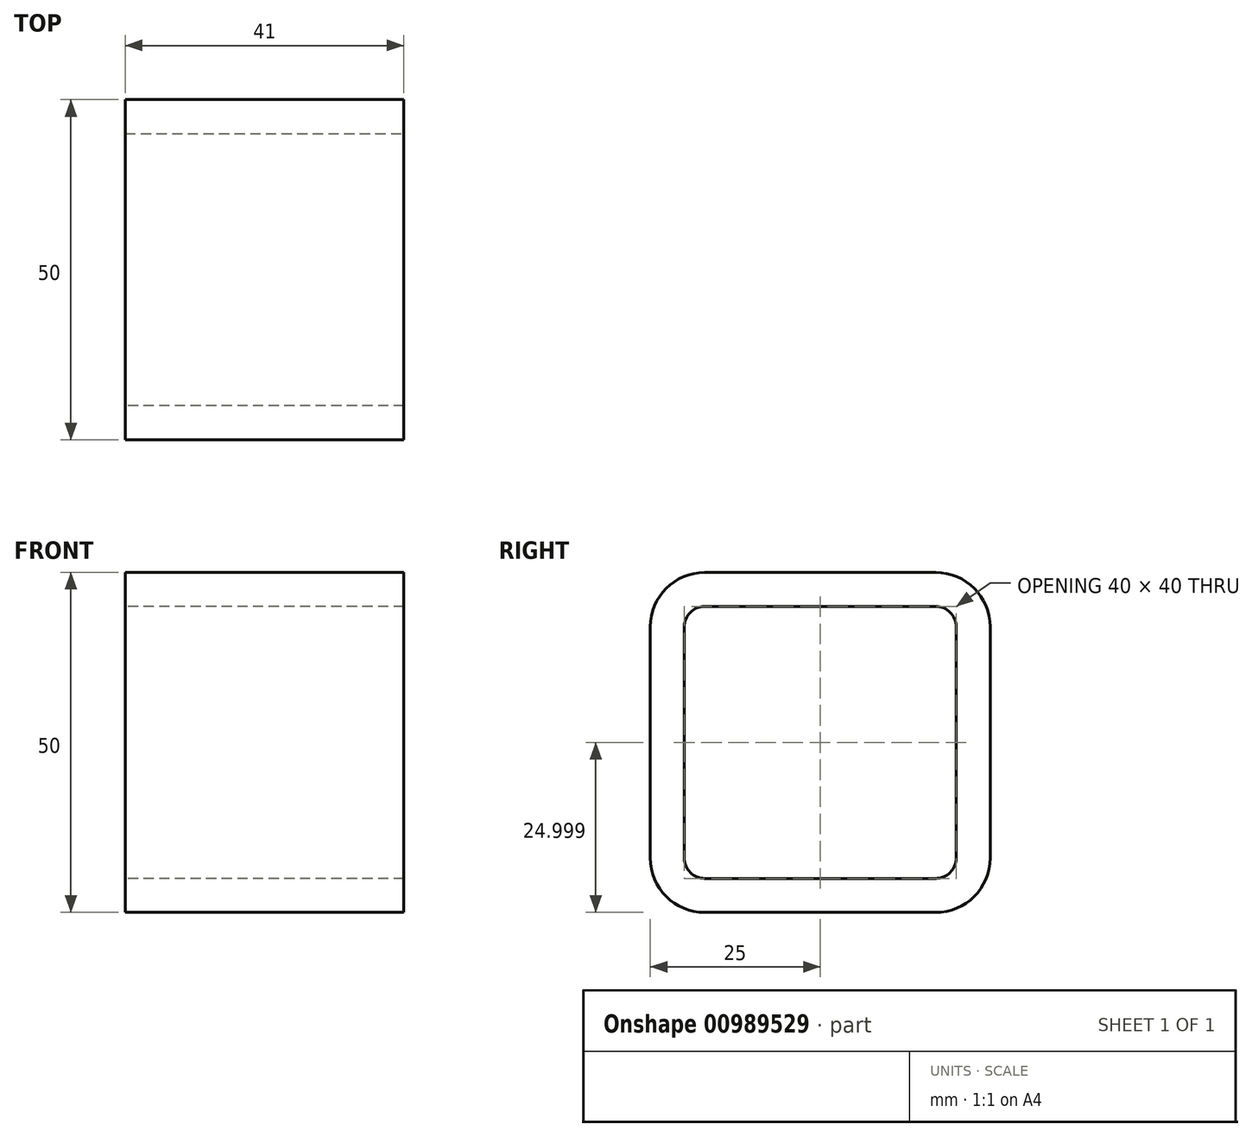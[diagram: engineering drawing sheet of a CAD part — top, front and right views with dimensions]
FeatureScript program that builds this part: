
annotation { "Feature Type Name" : "Feature", "Feature Type Description" : "" }
export const myFeature = defineFeature(function(context is Context, id is Id, definition is map)
    precondition{}
    {
        {
            var Q0;
            Q0=qCreatedBy(makeId("Right.planeOp"),FACE);
            var sketch = newSketch(context, id + "F0", { "sketchPlane" : qUnion([Q0])});
            skPoint(sketch, "E0.visualSharp", {"position": v(-30, 19.07) * mm});
            skPoint(sketch, "E1.visualSharp", {"position": v(20, 19.07) * mm});
            skPoint(sketch, "E2.visualSharp", {"position": v(20, -30.93) * mm});
            skPoint(sketch, "E3.visualSharp", {"position": v(-30, -30.93) * mm});
            skPoint(sketch, "E4.start.orphan", {"position": v(22, 25.88) * mm});
            skPoint(sketch, "E5.end.orphan", {"position": v(-25, -22) * mm});
            skPoint(sketch, "E5.start.orphan", {"position": v(-25, 22) * mm});
            skPoint(sketch, "E6.end.orphan", {"position": v(-22, -25) * mm});
            skPoint(sketch, "E6.start.orphan", {"position": v(12.4, -25) * mm});
            skPoint(sketch, "E7.start.orphan", {"position": v(25.62, 22) * mm});
            skPoint(sketch, "E1.filletArc.center.orphan", {"position": v(22, 22) * mm});
            skPoint(sketch, "E0.filletArc.center.orphan", {"position": v(-22, 22) * mm});
            skPoint(sketch, "E3.filletArc.center.orphan", {"position": v(-22, -22) * mm});
            skLineSegment(sketch, "E8.right", {"start": v(20, 11.07) * mm, "end": v(20, -22.93) * mm});
            skPoint(sketch, "E9.trimOffspring.start.orphan", {"position": v(22, 30) * mm});
            skPoint(sketch, "E10.trimOffspring.start.orphan", {"position": v(12.4, -30) * mm});
            skPoint(sketch, "E8.top.end.orphan", {"position": v(-22, -30) * mm});
            skLineSegment(sketch, "E11", {"start": v(12, 19.07) * mm, "end": v(-22, 19.07) * mm});
            skLineSegment(sketch, "E12", {"start": v(-22, -30.93) * mm, "end": v(12, -30.93) * mm});
            skLineSegment(sketch, "E13", {"start": v(-30, 11.07) * mm, "end": v(-30, -22.93) * mm});
            skLineSegment(sketch, "E14.bottom", {"start": v(-25, 14.07) * mm, "end": v(-25, 14.07) * mm});
            skLineSegment(sketch, "E14.top", {"start": v(-25, -25.93) * mm, "end": v(-25, -25.93) * mm});
            skLineSegment(sketch, "E14.left", {"start": v(-25, 11.07) * mm, "end": v(-25, -22.93) * mm});
            skLineSegment(sketch, "E14.right", {"start": v(-25, 11.07) * mm, "end": v(-25, -22.93) * mm});
            skLineSegment(sketch, "E15.bottom", {"start": v(-22, -25.93) * mm, "end": v(12, -25.93) * mm});
            skLineSegment(sketch, "E16.bottom", {"start": v(15, -25) * mm, "end": v(15, -25) * mm});
            skLineSegment(sketch, "E16.top", {"start": v(15, 14.07) * mm, "end": v(15, 14.07) * mm});
            skLineSegment(sketch, "E16.left", {"start": v(15, -22.93) * mm, "end": v(15, 11.07) * mm});
            skLineSegment(sketch, "E16.right", {"start": v(15, -22.93) * mm, "end": v(15, 11.07) * mm});
            skLineSegment(sketch, "E17.bottom", {"start": v(-22, 14.07) * mm, "end": v(12, 14.07) * mm});
            skLineSegment(sketch, "E17.top", {"start": v(-22, 14.07) * mm, "end": v(12, 14.07) * mm});
            skPoint(sketch, "E18.visualSharp", {"position": v(-25, 14.07) * mm});
            skArc(sketch, "E18.filletArc", {"start": v(-22, 14.07) * mm, "mid": v(-24.12, 13.2) * mm, "end": v(-25, 11.07) * mm});
            skPoint(sketch, "E19.visualSharp", {"position": v(15, 14.07) * mm});
            skArc(sketch, "E19.filletArc", {"start": v(15, 11.07) * mm, "mid": v(14.12, 13.2) * mm, "end": v(12, 14.07) * mm});
            skPoint(sketch, "E20.visualSharp", {"position": v(-25, -25.93) * mm});
            skArc(sketch, "E20.filletArc", {"start": v(-25, -22.93) * mm, "mid": v(-24.12, -25.05) * mm, "end": v(-22, -25.93) * mm});
            skArc(sketch, "E21.filletArc", {"start": v(12, -25.93) * mm, "mid": v(14.12, -25.05) * mm, "end": v(15, -22.93) * mm});
            skArc(sketch, "E22.filletArc", {"start": v(-22, 19.07) * mm, "mid": v(-27.66, 16.73) * mm, "end": v(-30, 11.07) * mm});
            skArc(sketch, "E23.filletArc", {"start": v(-30, -22.93) * mm, "mid": v(-27.66, -28.59) * mm, "end": v(-22, -30.93) * mm});
            skArc(sketch, "E24.filletArc", {"start": v(12, -30.93) * mm, "mid": v(17.66, -28.59) * mm, "end": v(20, -22.93) * mm});
            skArc(sketch, "E25.filletArc", {"start": v(20, 11.07) * mm, "mid": v(17.66, 16.73) * mm, "end": v(12, 19.07) * mm});
            skSolve(sketch);
        }
        {
            var Q0;
            Q0=makeQuery(id+"F0.imprint","IMPRINT",FACE,{"disambiguationData":[TD([[makeQuery(id+"F0.imprint","IMPRINT",EDGE,{"derivedFrom":sQuery(id+"F0.wireOp",EDGE,"E8.right")}),-1.0]])]});
            extrude(context, id + "F1", {"entities" : qUnion([Q0]), "depth" : 41 * mm, "offsetDistance" : 25 * mm, "hasDraft" : true, "draftAngle" : 0 * degree});
        }
    });
